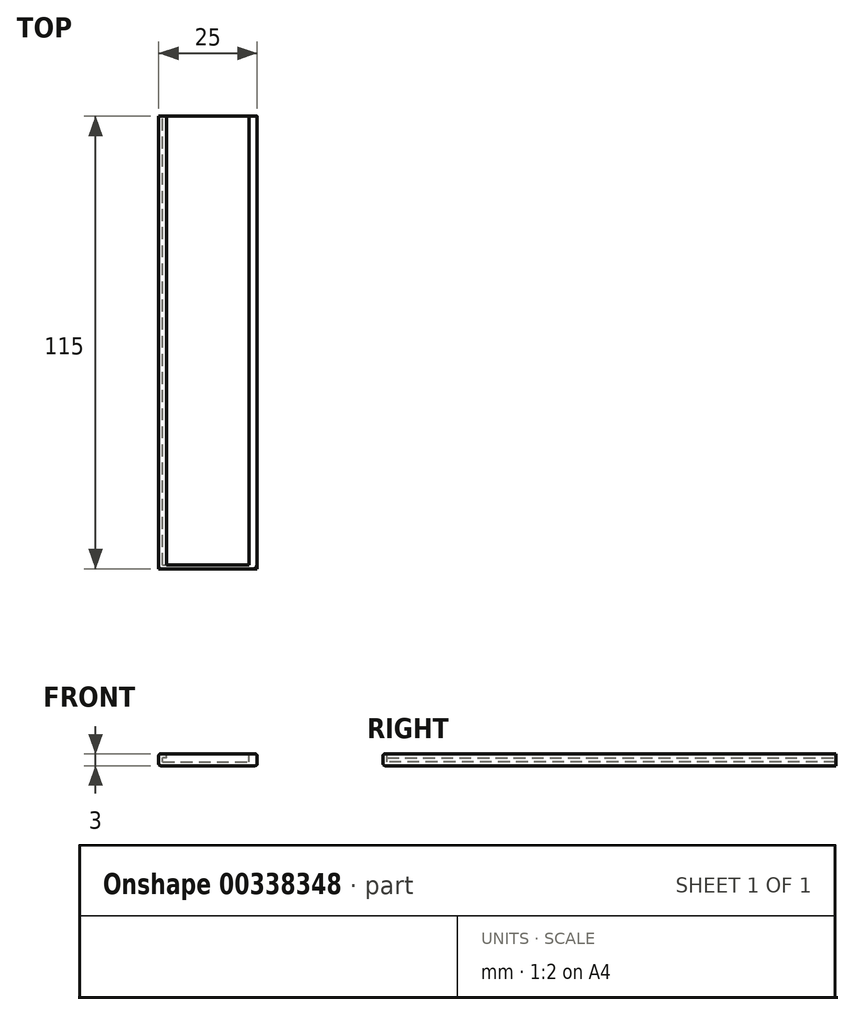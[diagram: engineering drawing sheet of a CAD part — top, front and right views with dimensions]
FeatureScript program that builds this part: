
annotation { "Feature Type Name" : "Feature", "Feature Type Description" : "" }
export const myFeature = defineFeature(function(context is Context, id is Id, definition is map)
    precondition{}
    {
        {
            var Q0;
            Q0=qCreatedBy(makeId("Top.planeOp"),FACE);
            var sketch = newSketch(context, id + "F0", { "sketchPlane" : qUnion([Q0])});
            skLineSegment(sketch, "E0.bottom", {"start": v(12.5, -57) * mm, "end": v(-12.5, -57) * mm});
            skLineSegment(sketch, "E0.top", {"start": v(12.5, 57) * mm, "end": v(-12.5, 57) * mm});
            skLineSegment(sketch, "E0.left", {"start": v(12.5, -57) * mm, "end": v(12.5, 57) * mm});
            skLineSegment(sketch, "E0.right", {"start": v(-12.5, -57) * mm, "end": v(-12.5, 57) * mm});
            skPoint(sketch, "E0.middle", {"position": v(0, 0) * mm});
            skSolve(sketch);
        }
        {
            var Q0;
            Q0=makeQuery(id+"F0.imprint","IMPRINT",FACE,{"disambiguationData":[TD([[makeQuery(id+"F0.imprint","IMPRINT",EDGE,{"derivedFrom":sQuery(id+"F0.wireOp",EDGE,"E0.bottom")}),-1.0]])]});
            extrude(context, id + "F1", {"entities" : qUnion([Q0]), "depth" : 3 * mm});
        }
        {
            var Q0;
            Q0=makeQuery(id+"F1.opExtrude","CAP_FACE",FACE,{"disambiguationData":[OSD([sQuery(id+"F0.wireOp",EDGE,"E0.bottom"),sQuery(id+"F0.wireOp",EDGE,"E0.top"),sQuery(id+"F0.wireOp",EDGE,"E0.left"),sQuery(id+"F0.wireOp",EDGE,"E0.right")])],"isStart":false});
            var sketch = newSketch(context, id + "F2", { "sketchPlane" : qUnion([Q0])});
            skLineSegment(sketch, "E1.bottom", {"start": v(-10.5, 57) * mm, "end": v(10.5, 57) * mm});
            skLineSegment(sketch, "E1.top", {"start": v(-10.5, -56) * mm, "end": v(10.5, -56) * mm});
            skLineSegment(sketch, "E1.left", {"start": v(-10.5, 57) * mm, "end": v(-10.5, -56) * mm});
            skLineSegment(sketch, "E1.right", {"start": v(10.5, 57) * mm, "end": v(10.5, -56) * mm});
            skSolve(sketch);
        }
        {
            var Q0;
            Q0=makeQuery(id+"F2.imprint","IMPRINT",FACE,{"disambiguationData":[TD([[makeQuery(id+"F2.imprint","IMPRINT",EDGE,{"derivedFrom":sQuery(id+"F2.wireOp",EDGE,"E1.bottom")}),1.0]])]});
            extrude(context, id + "F3", {"entities" : qUnion([Q0]), "operationType" : NewBodyOperationType.REMOVE, "oppositeDirection" : true, "depth" : 2 * mm});
        }
        {
            var Q0;
            Q0=makeQuery(id+"F1.opExtrude","SWEPT_FACE",FACE,{"disambiguationData":[OSD([sQuery(id+"F0.wireOp",EDGE,"E0.top")])]});
            var sketch = newSketch(context, id + "F4", { "sketchPlane" : qUnion([Q0])});
            skPoint(sketch, "E2.oppositeSnap0", {"position": v(11.5, 3) * mm});
            skLineSegment(sketch, "E2.bottom", {"start": v(10.5, 1) * mm, "end": v(11.5, 1) * mm});
            skLineSegment(sketch, "E2.top", {"start": v(10.5, 2) * mm, "end": v(11.5, 2) * mm});
            skLineSegment(sketch, "E2.left", {"start": v(10.5, 1) * mm, "end": v(10.5, 2) * mm});
            skLineSegment(sketch, "E2.right", {"start": v(11.5, 1) * mm, "end": v(11.5, 2) * mm});
            skSolve(sketch);
        }
        {
            var Q0;
            Q0=makeQuery(id+"F4.imprint","IMPRINT",FACE,{"disambiguationData":[TD([[makeQuery(id+"F4.imprint","IMPRINT",EDGE,{"derivedFrom":sQuery(id+"F4.wireOp",EDGE,"E2.bottom")}),1.0]])]});
            extrude(context, id + "F5", {"entities" : qUnion([Q0]), "operationType" : NewBodyOperationType.REMOVE, "oppositeDirection" : true, "depth" : 113 * mm});
        }
        {
            var Q0;
            Q0=makeQuery(id+"F1.opExtrude","SWEPT_FACE",FACE,{"disambiguationData":[OSD([sQuery(id+"F0.wireOp",EDGE,"E0.top")])]});
            extrude(context, id + "F6", {"entities" : qUnion([Q0]), "operationType" : NewBodyOperationType.ADD, "depth" : 1 * mm});
        }
        {
            var Q0;
            {var subQ0=sQuery(id+"F0.wireOp",EDGE,"E0.left");var subQ1=sQuery(id+"F0.wireOp",EDGE,"E0.top");Q0=makeQuery(id+"F6.boolean.opBoolean","MERGE",EDGE,{"derivedFrom":[makeQuery(id+"F1.opExtrude","CAP_EDGE",EDGE,{"disambiguationData":[OSD([subQ0])],"isStart":true}),makeQuery(id+"F6.opExtrude","SWEPT_EDGE",EDGE,{"disambiguationData":[OSD([subQ1,subQ0]),TDD([makeQuery(id+"F1.opExtrude","CAP_VERTEX",VERTEX,{"disambiguationData":[OSD([subQ1,subQ0])],"isStart":true})])]})]});}
            var Q1;
            {var subQ0=sQuery(id+"F0.wireOp",EDGE,"E0.left");var subQ1=sQuery(id+"F0.wireOp",EDGE,"E0.top");Q1=makeQuery(id+"F6.boolean.opBoolean","MERGE",EDGE,{"derivedFrom":[makeQuery(id+"F1.opExtrude","CAP_EDGE",EDGE,{"disambiguationData":[OSD([subQ0])],"isStart":false}),makeQuery(id+"F6.opExtrude","SWEPT_EDGE",EDGE,{"disambiguationData":[OSD([subQ1,subQ0]),TDD([makeQuery(id+"F1.opExtrude","CAP_VERTEX",VERTEX,{"disambiguationData":[OSD([subQ1,subQ0])],"isStart":false})])]})]});}
            var Q2;
            Q2=makeQuery(id+"F1.opExtrude","CAP_EDGE",EDGE,{"disambiguationData":[OSD([sQuery(id+"F0.wireOp",EDGE,"E0.bottom")])],"isStart":false});
            var Q3;
            Q3=makeQuery(id+"F1.opExtrude","CAP_EDGE",EDGE,{"disambiguationData":[OSD([sQuery(id+"F0.wireOp",EDGE,"E0.bottom")])],"isStart":true});
            var Q4;
            {var subQ0=sQuery(id+"F0.wireOp",EDGE,"E0.right");var subQ1=sQuery(id+"F0.wireOp",EDGE,"E0.top");Q4=makeQuery(id+"F6.boolean.opBoolean","MERGE",EDGE,{"derivedFrom":[makeQuery(id+"F1.opExtrude","CAP_EDGE",EDGE,{"disambiguationData":[OSD([subQ0])],"isStart":false}),makeQuery(id+"F6.opExtrude","SWEPT_EDGE",EDGE,{"disambiguationData":[OSD([subQ1,subQ0]),TDD([makeQuery(id+"F1.opExtrude","CAP_VERTEX",VERTEX,{"disambiguationData":[OSD([subQ1,subQ0])],"isStart":false})])]})]});}
            var Q5;
            {var subQ0=sQuery(id+"F0.wireOp",EDGE,"E0.right");var subQ1=sQuery(id+"F0.wireOp",EDGE,"E0.top");Q5=makeQuery(id+"F6.boolean.opBoolean","MERGE",EDGE,{"derivedFrom":[makeQuery(id+"F1.opExtrude","CAP_EDGE",EDGE,{"disambiguationData":[OSD([subQ0])],"isStart":true}),makeQuery(id+"F6.opExtrude","SWEPT_EDGE",EDGE,{"disambiguationData":[OSD([subQ1,subQ0]),TDD([makeQuery(id+"F1.opExtrude","CAP_VERTEX",VERTEX,{"disambiguationData":[OSD([subQ1,subQ0])],"isStart":true})])]})]});}
            fillet(context, id + "F7", {"entities" : qUnion([Q0, Q1, Q2, Q3, Q4, Q5]), "radius" : 0.5 * mm, "tangentPropagation" : true, "allowEdgeOverflow" : false});
        }
    });
